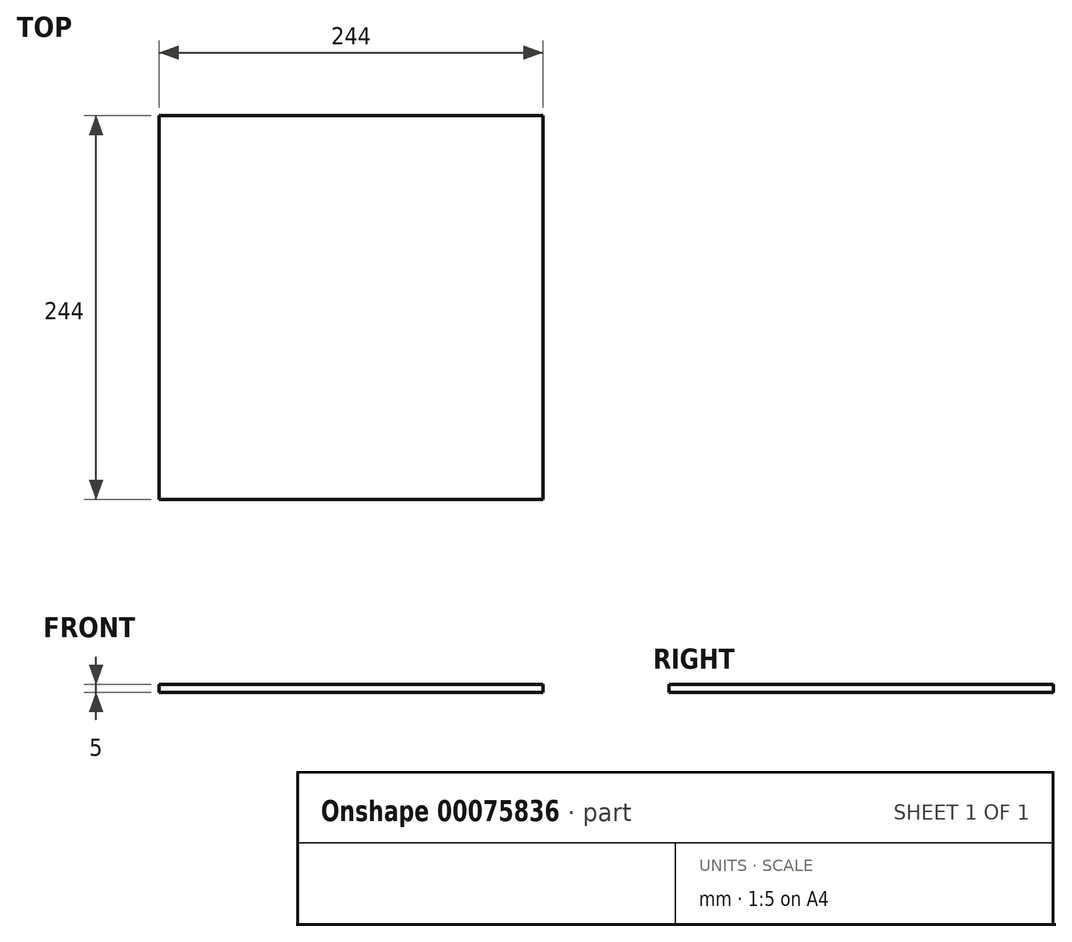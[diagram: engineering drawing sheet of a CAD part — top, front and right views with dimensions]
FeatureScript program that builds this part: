
annotation { "Feature Type Name" : "Feature", "Feature Type Description" : "" }
export const myFeature = defineFeature(function(context is Context, id is Id, definition is map)
    precondition{}
    {
        {
            var Q0;
            Q0=qCreatedBy(makeId("Top.planeOp"),FACE);
            var sketch = newSketch(context, id + "F0", { "sketchPlane" : qUnion([Q0])});
            skLineSegment(sketch, "E0.bottom", {"start": v(122, 122) * mm, "end": v(-122, 122) * mm});
            skLineSegment(sketch, "E0.top", {"start": v(122, -122) * mm, "end": v(-122, -122) * mm});
            skLineSegment(sketch, "E0.left", {"start": v(122, 122) * mm, "end": v(122, -122) * mm});
            skLineSegment(sketch, "E0.right", {"start": v(-122, 122) * mm, "end": v(-122, -122) * mm});
            skPoint(sketch, "E0.middle", {"position": v(0, 0) * mm});
            skSolve(sketch);
        }
        {
            var Q0;
            Q0=makeQuery(id+"F0.imprint","IMPRINT",FACE,{"disambiguationData":[TD([[makeQuery(id+"F0.imprint","IMPRINT",EDGE,{"derivedFrom":sQuery(id+"F0.wireOp",EDGE,"E0.bottom")}),1.0]])]});
            extrude(context, id + "F1", {"entities" : qUnion([Q0]), "depth" : 5 * mm});
        }
    });
